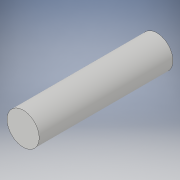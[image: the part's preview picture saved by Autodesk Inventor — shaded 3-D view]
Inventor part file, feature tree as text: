
AUTODESK INVENTOR PART (.ipt)
format: ipt  version: 2017 (Build 210142000, 142)  size: 88,576 bytes
history: native  units: in
note: dims shown in document units (in); Inventor stores cm internally (conversion verified against a paired STEP export)
features: extrude x1, sketch x1
ambient origin geometry x8: Origin, YZ Plane, XZ Plane, XY Plane, X Axis, Y Axis, Z Axis, Center Point
bodies: Solid1 (feature_tree)
feature tree (2):
  extrude  "Extrusion1"  Depth=1.9685in TaperAngle=0.0deg
  sketch  "Sketch1"  dims[d0=0.4724in d1=1.9685in d2=0.0in]
